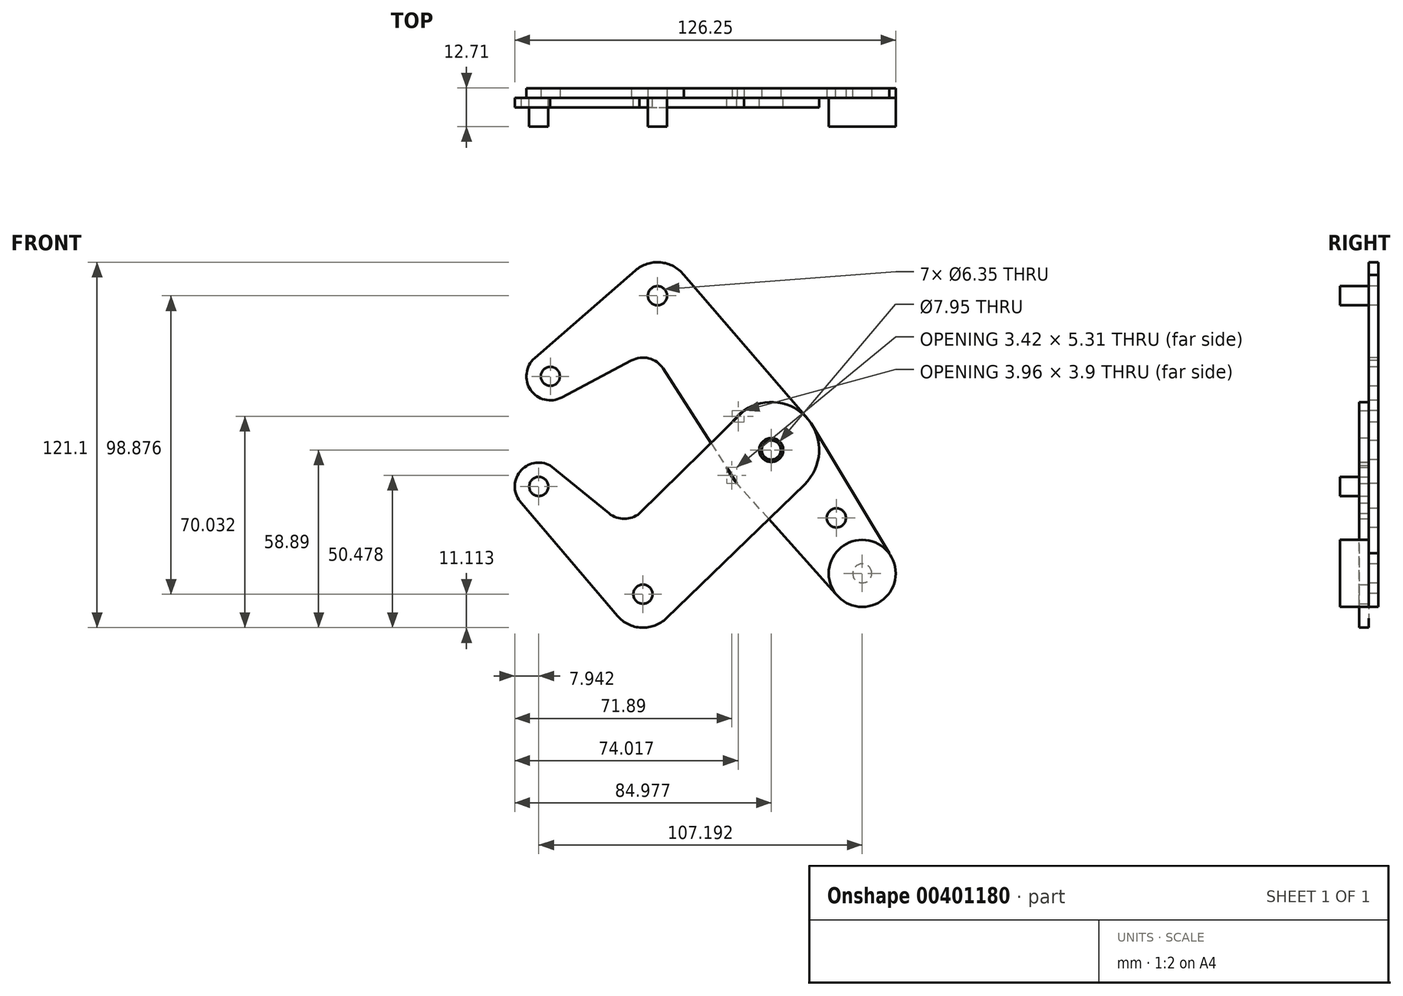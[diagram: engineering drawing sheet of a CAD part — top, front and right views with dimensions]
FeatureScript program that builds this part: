
annotation { "Feature Type Name" : "Feature", "Feature Type Description" : "" }
export const myFeature = defineFeature(function(context is Context, id is Id, definition is map)
    precondition{}
    {
        {
            var Q0;
            Q0=qCreatedBy(makeId("Front.planeOp"),FACE);
            var sketch = newSketch(context, id + "F0", { "sketchPlane" : qUnion([Q0])});
            skCircle(sketch, "E0", {"center": v(-14.02, 56.23) * mm, "radius": 11.11 * mm});
            skCircle(sketch, "E1", {"center": v(-49.53, 29.54) * mm, "radius": 7.94 * mm});
            skCircle(sketch, "E2", {"center": v(53.83, -35.75) * mm, "radius": 11.11 * mm});
            skCircle(sketch, "E3", {"center": v(23.68, 5.13) * mm, "radius": 15.88 * mm});
            skCircle(sketch, "E4", {"center": v(-49.53, 29.54) * mm, "radius": 3.18 * mm});
            skCircle(sketch, "E5", {"center": v(-14.02, 56.23) * mm, "radius": 3.18 * mm});
            skCircle(sketch, "E6", {"center": v(23.68, 5.13) * mm, "radius": 3.98 * mm});
            skCircle(sketch, "E7", {"center": v(23.68, 5.13) * mm, "radius": 3.18 * mm});
            skCircle(sketch, "E8", {"center": v(53.83, -35.75) * mm, "radius": 3.18 * mm});
            skCircle(sketch, "E9", {"center": v(45.26, -17.38) * mm, "radius": 3.18 * mm});
            skCircle(sketch, "E10", {"center": v(-18.83, -42.65) * mm, "radius": 11.11 * mm});
            skCircle(sketch, "E11", {"center": v(-53.36, -6.97) * mm, "radius": 7.94 * mm});
            skLineSegment(sketch, "E12", {"start": v(-54.74, 35.53) * mm, "end": v(-21.31, 64.61) * mm});
            skLineSegment(sketch, "E13", {"start": v(-59.17, -12.37) * mm, "end": v(-27.3, -49.85) * mm});
            skLineSegment(sketch, "E14", {"start": v(62.73, -29.1) * mm, "end": v(37.29, 13.3) * mm});
            skLineSegment(sketch, "E15", {"start": v(-5.31, 63.13) * mm, "end": v(35.7, 15.49) * mm});
            skLineSegment(sketch, "E16", {"start": v(44.9, -42.36) * mm, "end": v(12.34, -6.01) * mm});
            skLineSegment(sketch, "E17", {"start": v(-11.08, -50.6) * mm, "end": v(41.2, 0) * mm});
            skLineSegment(sketch, "E18", {"start": v(-49.56, 0) * mm, "end": v(-30.04, -15.9) * mm});
            skArc(sketch, "E19", {"start": v(-30.04, -15.9) * mm, "mid": v(-25.02, -17.69) * mm, "end": v(-20, -15.9) * mm});
            skLineSegment(sketch, "E20", {"start": v(-20, -15.9) * mm, "end": v(14.7, 18.22) * mm});
            skLineSegment(sketch, "E21", {"start": v(-12.14, 32.09) * mm, "end": v(12.34, -6.01) * mm});
            skArc(sketch, "E22", {"start": v(-12.14, 32.09) * mm, "mid": v(-16.86, 35.5) * mm, "end": v(-22.63, 34.78) * mm});
            skLineSegment(sketch, "E23", {"start": v(-22.63, 34.78) * mm, "end": v(-45.82, 22.52) * mm});
            skCircle(sketch, "E24", {"center": v(-53.36, -6.97) * mm, "radius": 3.18 * mm});
            skCircle(sketch, "E25", {"center": v(-18.83, -42.65) * mm, "radius": 3.18 * mm});
            skLineSegment(sketch, "E26", {"start": v(-10.12, -35.75) * mm, "end": v(-10.12, -49.54) * mm});
            skSolve(sketch);
        }
        {
            var Q0;
            {var subQ5=sQuery(id+"F0.wireOp",EDGE,"E12");Q0=makeQuery(id+"F0.imprint","IMPRINT",FACE,{"disambiguationData":[TD([[makeQuery(id+"F0.imprint","IMPRINT",EDGE,{"derivedFrom":subQ5}),-1.0]])]});}
            var Q1;
            Q1=makeQuery(id+"F0.imprint","IMPRINT",FACE,{"disambiguationData":[TD([[makeQuery(id+"F0.imprint","IMPRINT",EDGE,{"derivedFrom":sQuery(id+"F0.wireOp",EDGE,"E4")}),-1.0]])]});
            var Q2;
            Q2=makeQuery(id+"F0.imprint","IMPRINT",FACE,{"disambiguationData":[TD([[makeQuery(id+"F0.imprint","IMPRINT",EDGE,{"derivedFrom":sQuery(id+"F0.wireOp",EDGE,"E9")}),-1.0]])]});
            var Q3;
            Q3=makeQuery(id+"F0.imprint","IMPRINT",FACE,{"disambiguationData":[TD([[makeQuery(id+"F0.imprint","IMPRINT",EDGE,{"derivedFrom":sQuery(id+"F0.wireOp",EDGE,"E8")}),-1.0]])]});
            var Q4;
            {var subQ0=sQuery(id+"F0.wireOp",EDGE,"E17");var subQ1=sQuery(id+"F0.wireOp",EDGE,"E3");var subQ2=makeQuery(id+"F0.imprint","INTERSECT",VERTEX,{"derivedFrom":[subQ1,subQ0]});Q4=makeQuery(id+"F0.imprint","IMPRINT",FACE,{"disambiguationData":[TD([[makeQuery(id+"F0.imprint","IMPRINT",EDGE,{"disambiguationData":[TD([[subQ2,1.0]])],"derivedFrom":subQ1}),-1.0]])]});}
            var Q5;
            {var subQ0=sQuery(id+"F0.wireOp",EDGE,"E20");var subQ1=sQuery(id+"F0.wireOp",EDGE,"E3");var subQ2=makeQuery(id+"F0.imprint","INTERSECT",VERTEX,{"disambiguationData":[OD(1.0)],"derivedFrom":[subQ1,subQ0]});Q5=makeQuery(id+"F0.imprint","IMPRINT",FACE,{"disambiguationData":[TD([[makeQuery(id+"F0.imprint","IMPRINT",EDGE,{"disambiguationData":[TD([[subQ2,-1.0]])],"derivedFrom":subQ1}),-1.0]])]});}
            var Q6;
            Q6=makeQuery(id+"F0.imprint","IMPRINT",FACE,{"disambiguationData":[TD([[makeQuery(id+"F0.imprint","IMPRINT",EDGE,{"derivedFrom":sQuery(id+"F0.wireOp",EDGE,"E5")}),-1.0]])]});
            var Q7;
            Q7=makeQuery(id+"F0.imprint","IMPRINT",FACE,{"disambiguationData":[TD([[makeQuery(id+"F0.imprint","IMPRINT",EDGE,{"derivedFrom":sQuery(id+"F0.wireOp",EDGE,"E6")}),1.0]])]});
            var Q8;
            Q8=makeQuery(id+"F0.imprint","IMPRINT",FACE,{"disambiguationData":[TD([[makeQuery(id+"F0.imprint","IMPRINT",EDGE,{"derivedFrom":sQuery(id+"F0.wireOp",EDGE,"E6")}),-1.0]])]});
            extrude(context, id + "F1", {"entities" : qUnion([Q0, Q1, Q2, Q3, Q4, Q5, Q6, Q7, Q8]), "oppositeDirection" : true, "depth" : 3.17 * mm});
        }
        {
            var Q0;
            Q0=makeQuery(id+"F0.imprint","IMPRINT",FACE,{"disambiguationData":[TD([[makeQuery(id+"F0.imprint","IMPRINT",EDGE,{"derivedFrom":sQuery(id+"F0.wireOp",EDGE,"E6")}),-1.0]])]});
            var Q1;
            {var subQ0=sQuery(id+"F0.wireOp",EDGE,"E20");var subQ1=sQuery(id+"F0.wireOp",EDGE,"E3");var subQ2=makeQuery(id+"F0.imprint","INTERSECT",VERTEX,{"disambiguationData":[OD(1.0)],"derivedFrom":[subQ1,subQ0]});Q1=makeQuery(id+"F0.imprint","IMPRINT",FACE,{"disambiguationData":[TD([[makeQuery(id+"F0.imprint","IMPRINT",EDGE,{"disambiguationData":[TD([[subQ2,-1.0]])],"derivedFrom":subQ1}),-1.0]])]});}
            var Q2;
            {var subQ0=sQuery(id+"F0.wireOp",EDGE,"E17");var subQ1=sQuery(id+"F0.wireOp",EDGE,"E3");var subQ2=makeQuery(id+"F0.imprint","INTERSECT",VERTEX,{"derivedFrom":[subQ1,subQ0]});Q2=makeQuery(id+"F0.imprint","IMPRINT",FACE,{"disambiguationData":[TD([[makeQuery(id+"F0.imprint","IMPRINT",EDGE,{"disambiguationData":[TD([[subQ2,1.0]])],"derivedFrom":subQ1}),-1.0]])]});}
            var Q3;
            {var subQ9=sQuery(id+"F0.wireOp",EDGE,"E13");Q3=makeQuery(id+"F0.imprint","IMPRINT",FACE,{"disambiguationData":[TD([[makeQuery(id+"F0.imprint","IMPRINT",EDGE,{"derivedFrom":subQ9}),1.0]])]});}
            var Q4;
            {var subQ0=sQuery(id+"F0.wireOp",EDGE,"E26");Q4=makeQuery(id+"F0.imprint","IMPRINT",FACE,{"disambiguationData":[TD([[makeQuery(id+"F0.imprint","IMPRINT",EDGE,{"derivedFrom":subQ0}),1.0]])]});}
            var Q5;
            Q5=makeQuery(id+"F0.imprint","IMPRINT",FACE,{"disambiguationData":[TD([[makeQuery(id+"F0.imprint","IMPRINT",EDGE,{"derivedFrom":sQuery(id+"F0.wireOp",EDGE,"E25")}),-1.0]])]});
            var Q6;
            Q6=makeQuery(id+"F0.imprint","IMPRINT",FACE,{"disambiguationData":[TD([[makeQuery(id+"F0.imprint","IMPRINT",EDGE,{"derivedFrom":sQuery(id+"F0.wireOp",EDGE,"E24")}),-1.0]])]});
            extrude(context, id + "F2", {"entities" : qUnion([Q0, Q1, Q2, Q3, Q4, Q5, Q6]), "depth" : 3.17 * mm});
        }
        {
            var Q0;
            Q0=qCreatedBy(makeId("Front.planeOp"),FACE);
            cPlane(context, id + "F3", {"entities" : qUnion([Q0]), "cplaneType" : CPlaneType.OFFSET, "offset" : 9.52 * mm, "width" : 152.4 * mm, "height" : 152.4 * mm});
        }
        {
            var Q0;
            Q0=makeQuery(id+"F0.imprint","IMPRINT",FACE,{"disambiguationData":[TD([[makeQuery(id+"F0.imprint","IMPRINT",EDGE,{"derivedFrom":sQuery(id+"F0.wireOp",EDGE,"E5")}),1.0]])]});
            var Q1;
            Q1=makeQuery(id+"F0.imprint","IMPRINT",FACE,{"disambiguationData":[TD([[makeQuery(id+"F0.imprint","IMPRINT",EDGE,{"derivedFrom":sQuery(id+"F0.wireOp",EDGE,"E8")}),-1.0]])]});
            var Q2;
            Q2=makeQuery(id+"F0.imprint","IMPRINT",FACE,{"disambiguationData":[TD([[makeQuery(id+"F0.imprint","IMPRINT",EDGE,{"derivedFrom":sQuery(id+"F0.wireOp",EDGE,"E8")}),1.0]])]});
            var Q3;
            Q3=makeQuery(id+"F0.imprint","IMPRINT",FACE,{"disambiguationData":[TD([[makeQuery(id+"F0.imprint","IMPRINT",EDGE,{"derivedFrom":sQuery(id+"F0.wireOp",EDGE,"E24")}),1.0]])]});
            var Q4;
            Q4=qCreatedBy(id+"F3.planeOp",FACE);
            extrude(context, id + "F4", {"entities" : qUnion([Q0, Q1, Q2, Q3]), "endBound" : BoundingType.UP_TO_SURFACE, "endBoundEntityFace" : qUnion([Q4]), "depth" : 25.4 * mm});
        }
    });
